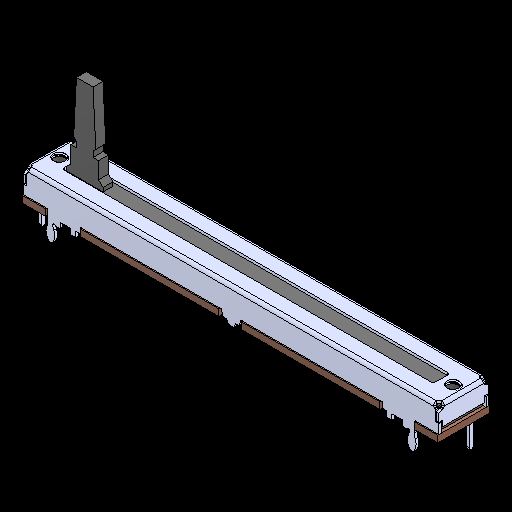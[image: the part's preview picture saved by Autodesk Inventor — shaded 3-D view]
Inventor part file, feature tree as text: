
AUTODESK INVENTOR PART (.ipt)
format: ipt  version: 2023.2 (Build 272271030, 271C)  size: 385,536 bytes
history: native  units: mm
features: other x3, fillet x3
ambient origin geometry x8: Origin, YZ Plane, XZ Plane, XY Plane, X Axis, Y Axis, Z Axis, Center Point
bodies: Solid1 (feature_tree), Solid2 (feature_tree), Solid3 (feature_tree), Solid4 (feature_tree), Solid5 (feature_tree), Solid6 (feature_tree)
feature tree (6):
  other  "Tab6"
  other  "Cut-Extrude5"
  fillet  "Fillet2"  [1 undecoded]
  fillet  "Fillet1"  [1 undecoded]
  fillet  "Fillet3"  [1 undecoded]
  other  "Boss-Extrude6"
note: 3 required parameter values undecoded (feature->parameter linkage not recoverable at this tier; creation-order binding heuristic only, values carry confidence <= 0.55)
